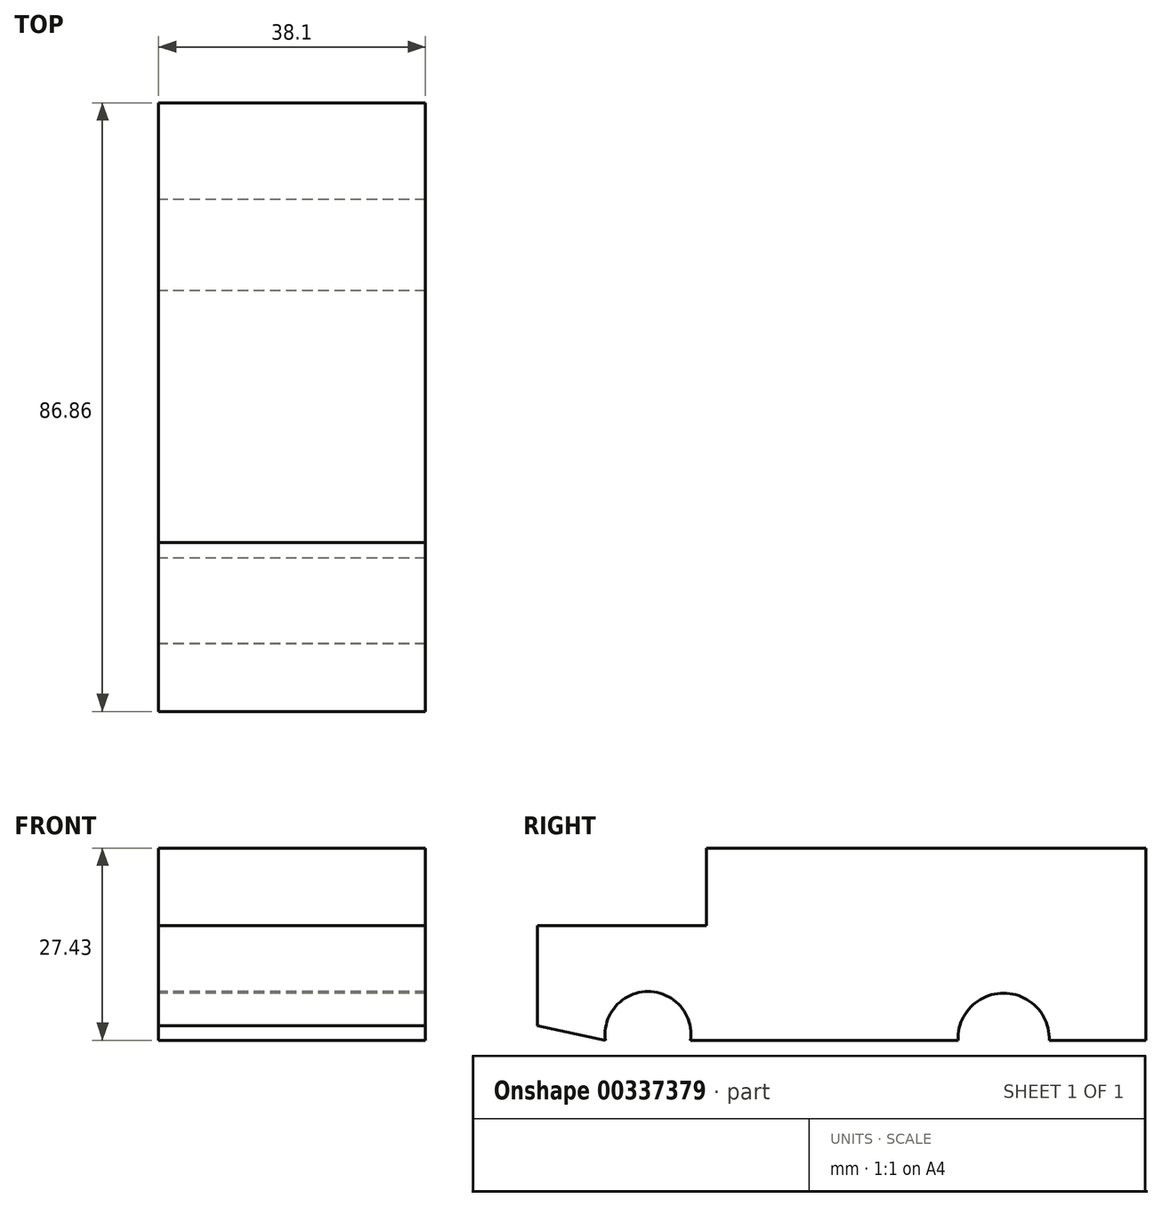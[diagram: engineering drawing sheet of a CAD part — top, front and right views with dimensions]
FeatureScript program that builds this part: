
annotation { "Feature Type Name" : "Feature", "Feature Type Description" : "" }
export const myFeature = defineFeature(function(context is Context, id is Id, definition is map)
    precondition{}
    {
        {
            var Q0;
            Q0=qCreatedBy(makeId("Right.planeOp"),FACE);
            var sketch = newSketch(context, id + "F0", { "sketchPlane" : qUnion([Q0])});
            skLineSegment(sketch, "E0", {"start": v(-46.9, 17.21) * mm, "end": v(-46.9, 31.53) * mm});
            skLineSegment(sketch, "E1", {"start": v(-46.9, 31.53) * mm, "end": v(-22.77, 31.53) * mm});
            skLineSegment(sketch, "E2", {"start": v(-22.77, 31.53) * mm, "end": v(-22.77, 42.59) * mm});
            skLineSegment(sketch, "E3", {"start": v(-22.77, 42.59) * mm, "end": v(39.96, 42.59) * mm});
            skLineSegment(sketch, "E4", {"start": v(39.96, 42.59) * mm, "end": v(39.96, 15.16) * mm});
            skLineSegment(sketch, "E5", {"start": v(39.96, 15.16) * mm, "end": v(26.16, 15.16) * mm});
            skArc(sketch, "E6", {"start": v(26.16, 15.16) * mm, "mid": v(19.64, 21.88) * mm, "end": v(13.13, 15.16) * mm});
            skLineSegment(sketch, "E7", {"start": v(13.13, 15.16) * mm, "end": v(-25.05, 15.16) * mm});
            skArc(sketch, "E8", {"start": v(-25.05, 15.16) * mm, "mid": v(-31.13, 22.1) * mm, "end": v(-37.2, 15.16) * mm});
            skLineSegment(sketch, "E9", {"start": v(-46.9, 17.21) * mm, "end": v(-37.2, 15.16) * mm});
            skSolve(sketch);
        }
        {
            var Q0;
            Q0 = qSketchRegion(id + "F0", true);
            extrude(context, id + "F1", {"entities" : qUnion([Q0]), "depth" : 38.1 * mm});
        }
    });
